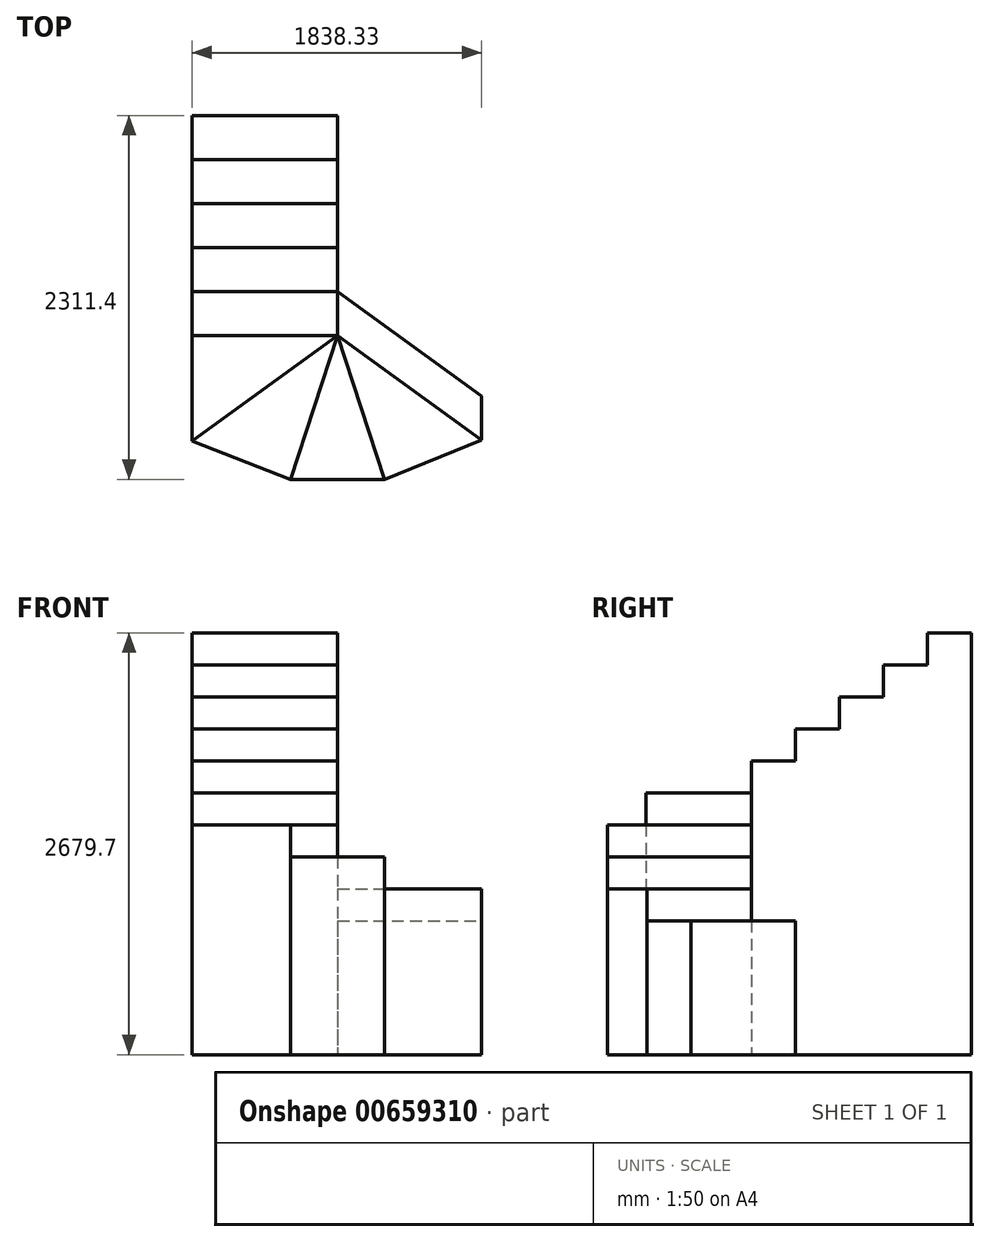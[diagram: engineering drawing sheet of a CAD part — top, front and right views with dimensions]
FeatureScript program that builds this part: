
annotation { "Feature Type Name" : "Feature", "Feature Type Description" : "" }
export const myFeature = defineFeature(function(context is Context, id is Id, definition is map)
    precondition{}
    {
        {
            var Q0;
            Q0=qCreatedBy(makeId("Top.planeOp"),FACE);
            var sketch = newSketch(context, id + "F0", { "sketchPlane" : qUnion([Q0])});
            skLineSegment(sketch, "E0.bottom", {"start": v(0, 0) * mm, "end": v(923.92, 0) * mm});
            skLineSegment(sketch, "E0.top", {"start": v(0, -279.4) * mm, "end": v(923.93, -279.4) * mm});
            skLineSegment(sketch, "E0.left", {"start": v(0, 0) * mm, "end": v(0, -279.4) * mm});
            skLineSegment(sketch, "E0.right", {"start": v(923.92, 0) * mm, "end": v(923.92, -279.4) * mm});
            skLineSegment(sketch, "E1.top", {"start": v(0, -558.8) * mm, "end": v(923.93, -558.8) * mm});
            skLineSegment(sketch, "E1.left", {"start": v(0, -279.4) * mm, "end": v(0, -558.8) * mm});
            skLineSegment(sketch, "E1.right", {"start": v(923.93, -279.4) * mm, "end": v(923.93, -558.8) * mm});
            skLineSegment(sketch, "E2.top", {"start": v(0, -838.2) * mm, "end": v(923.93, -838.2) * mm});
            skLineSegment(sketch, "E2.left", {"start": v(0, -558.8) * mm, "end": v(0, -838.2) * mm});
            skLineSegment(sketch, "E2.right", {"start": v(923.93, -558.8) * mm, "end": v(923.93, -838.2) * mm});
            skLineSegment(sketch, "E3.top", {"start": v(0, -1117.6) * mm, "end": v(923.93, -1117.6) * mm});
            skLineSegment(sketch, "E3.left", {"start": v(0, -838.2) * mm, "end": v(0, -1117.6) * mm});
            skLineSegment(sketch, "E3.right", {"start": v(923.93, -838.2) * mm, "end": v(923.93, -1117.6) * mm});
            skSolve(sketch);
        }
        {
            var Q0;
            Q0=makeQuery(id+"F0.imprint","IMPRINT",FACE,{"disambiguationData":[TD([[makeQuery(id+"F0.imprint","IMPRINT",EDGE,{"derivedFrom":sQuery(id+"F0.wireOp",EDGE,"E0.bottom")}),-1.0]])]});
            extrude(context, id + "F1", {"entities" : qUnion([Q0]), "depth" : 2679.7 * mm, "offsetDistance" : 25.4 * mm});
        }
        {
            var Q0;
            Q0=makeQuery(id+"F1.opExtrude","CAP_FACE",FACE,{"disambiguationData":[OSD([sQuery(id+"F0.wireOp",EDGE,"E0.bottom"),sQuery(id+"F0.wireOp",EDGE,"E0.left"),sQuery(id+"F0.wireOp",EDGE,"E0.right"),sQuery(id+"F0.wireOp",EDGE,"E0.top")])],"isStart":true});
            var sketch = newSketch(context, id + "F2", { "sketchPlane" : qUnion([Q0])});
            skLineSegment(sketch, "E4.bottom", {"start": v(0, 279.4) * mm, "end": v(923.92, 279.4) * mm});
            skLineSegment(sketch, "E4.top", {"start": v(0, 558.8) * mm, "end": v(923.92, 558.8) * mm});
            skLineSegment(sketch, "E4.left", {"start": v(0, 279.4) * mm, "end": v(0, 558.8) * mm});
            skLineSegment(sketch, "E4.right", {"start": v(923.92, 279.4) * mm, "end": v(923.92, 558.8) * mm});
            skSolve(sketch);
        }
        {
            var Q0;
            Q0 = qSketchRegion(id + "F2", true);
            extrude(context, id + "F3", {"entities" : qUnion([Q0]), "operationType" : NewBodyOperationType.ADD, "oppositeDirection" : true, "depth" : 2476.5 * mm, "offsetDistance" : 25.4 * mm});
        }
        {
            var Q0;
            Q0=makeQuery(id+"F3.boolean.opBoolean","MERGE",FACE,{"derivedFrom":[makeQuery(id+"F1.opExtrude","CAP_FACE",FACE,{"disambiguationData":[OSD([sQuery(id+"F0.wireOp",EDGE,"E0.bottom"),sQuery(id+"F0.wireOp",EDGE,"E0.left"),sQuery(id+"F0.wireOp",EDGE,"E0.right"),sQuery(id+"F0.wireOp",EDGE,"E0.top")])],"isStart":true}),makeQuery(id+"F3.opExtrude","CAP_FACE",FACE,{"disambiguationData":[OSD([sQuery(id+"F2.wireOp",EDGE,"E4.bottom"),sQuery(id+"F2.wireOp",EDGE,"E4.top"),sQuery(id+"F2.wireOp",EDGE,"E4.left"),sQuery(id+"F2.wireOp",EDGE,"E4.right")])],"isStart":true})]});
            var sketch = newSketch(context, id + "F4", { "sketchPlane" : qUnion([Q0])});
            skLineSegment(sketch, "E5.bottom", {"start": v(0, 558.8) * mm, "end": v(923.92, 558.8) * mm});
            skLineSegment(sketch, "E5.top", {"start": v(0, 838.2) * mm, "end": v(923.92, 838.2) * mm});
            skLineSegment(sketch, "E5.left", {"start": v(0, 558.8) * mm, "end": v(0, 838.2) * mm});
            skLineSegment(sketch, "E5.right", {"start": v(923.92, 558.8) * mm, "end": v(923.92, 838.2) * mm});
            skSolve(sketch);
        }
        {
            var Q0;
            Q0 = qSketchRegion(id + "F4", true);
            extrude(context, id + "F5", {"entities" : qUnion([Q0]), "operationType" : NewBodyOperationType.ADD, "oppositeDirection" : true, "depth" : 2273.3 * mm, "offsetDistance" : 25.4 * mm});
        }
        {
            var Q0;
            Q0=makeQuery(id+"F5.boolean.opBoolean","MERGE",FACE,{"derivedFrom":[makeQuery(id+"F3.boolean.opBoolean","MERGE",FACE,{"derivedFrom":[makeQuery(id+"F1.opExtrude","CAP_FACE",FACE,{"disambiguationData":[OSD([sQuery(id+"F0.wireOp",EDGE,"E0.bottom"),sQuery(id+"F0.wireOp",EDGE,"E0.left"),sQuery(id+"F0.wireOp",EDGE,"E0.right"),sQuery(id+"F0.wireOp",EDGE,"E0.top")])],"isStart":true}),makeQuery(id+"F3.opExtrude","CAP_FACE",FACE,{"disambiguationData":[OSD([sQuery(id+"F2.wireOp",EDGE,"E4.bottom"),sQuery(id+"F2.wireOp",EDGE,"E4.top"),sQuery(id+"F2.wireOp",EDGE,"E4.left"),sQuery(id+"F2.wireOp",EDGE,"E4.right")])],"isStart":true})]}),makeQuery(id+"F5.opExtrude","CAP_FACE",FACE,{"disambiguationData":[OSD([sQuery(id+"F4.wireOp",EDGE,"E5.bottom"),sQuery(id+"F4.wireOp",EDGE,"E5.top"),sQuery(id+"F4.wireOp",EDGE,"E5.left"),sQuery(id+"F4.wireOp",EDGE,"E5.right")])],"isStart":true})]});
            var sketch = newSketch(context, id + "F6", { "sketchPlane" : qUnion([Q0])});
            skLineSegment(sketch, "E6.bottom", {"start": v(923.92, 838.2) * mm, "end": v(0, 838.2) * mm});
            skLineSegment(sketch, "E6.top", {"start": v(923.92, 1117.6) * mm, "end": v(0, 1117.6) * mm});
            skLineSegment(sketch, "E6.left", {"start": v(923.92, 838.2) * mm, "end": v(923.92, 1117.6) * mm});
            skLineSegment(sketch, "E6.right", {"start": v(0, 838.2) * mm, "end": v(0, 1117.6) * mm});
            skSolve(sketch);
        }
        {
            var Q0;
            Q0 = qSketchRegion(id + "F6", true);
            extrude(context, id + "F7", {"entities" : qUnion([Q0]), "operationType" : NewBodyOperationType.ADD, "oppositeDirection" : true, "depth" : 2070.1 * mm, "offsetDistance" : 25.4 * mm});
        }
        {
            var Q0;
            Q0=makeQuery(id+"F7.boolean.opBoolean","MERGE",FACE,{"derivedFrom":[makeQuery(id+"F5.boolean.opBoolean","MERGE",FACE,{"derivedFrom":[makeQuery(id+"F3.boolean.opBoolean","MERGE",FACE,{"derivedFrom":[makeQuery(id+"F1.opExtrude","CAP_FACE",FACE,{"disambiguationData":[OSD([sQuery(id+"F0.wireOp",EDGE,"E0.bottom"),sQuery(id+"F0.wireOp",EDGE,"E0.left"),sQuery(id+"F0.wireOp",EDGE,"E0.right"),sQuery(id+"F0.wireOp",EDGE,"E0.top")])],"isStart":true}),makeQuery(id+"F3.opExtrude","CAP_FACE",FACE,{"disambiguationData":[OSD([sQuery(id+"F2.wireOp",EDGE,"E4.bottom"),sQuery(id+"F2.wireOp",EDGE,"E4.top"),sQuery(id+"F2.wireOp",EDGE,"E4.left"),sQuery(id+"F2.wireOp",EDGE,"E4.right")])],"isStart":true})]}),makeQuery(id+"F5.opExtrude","CAP_FACE",FACE,{"disambiguationData":[OSD([sQuery(id+"F4.wireOp",EDGE,"E5.bottom"),sQuery(id+"F4.wireOp",EDGE,"E5.top"),sQuery(id+"F4.wireOp",EDGE,"E5.left"),sQuery(id+"F4.wireOp",EDGE,"E5.right")])],"isStart":true})]}),makeQuery(id+"F7.opExtrude","CAP_FACE",FACE,{"disambiguationData":[OSD([sQuery(id+"F6.wireOp",EDGE,"E6.bottom"),sQuery(id+"F6.wireOp",EDGE,"E6.top"),sQuery(id+"F6.wireOp",EDGE,"E6.left"),sQuery(id+"F6.wireOp",EDGE,"E6.right")])],"isStart":true})]});
            var sketch = newSketch(context, id + "F8", { "sketchPlane" : qUnion([Q0])});
            skLineSegment(sketch, "E7.bottom", {"start": v(0, 1117.6) * mm, "end": v(923.92, 1117.6) * mm});
            skLineSegment(sketch, "E7.top", {"start": v(0, 1397) * mm, "end": v(923.92, 1397) * mm});
            skLineSegment(sketch, "E7.left", {"start": v(0, 1117.6) * mm, "end": v(0, 1397) * mm});
            skLineSegment(sketch, "E7.right", {"start": v(923.92, 1117.6) * mm, "end": v(923.92, 1397) * mm});
            skSolve(sketch);
        }
        {
            var Q0;
            Q0 = qSketchRegion(id + "F8", true);
            extrude(context, id + "F9", {"entities" : qUnion([Q0]), "operationType" : NewBodyOperationType.ADD, "oppositeDirection" : true, "depth" : 1866.9 * mm, "offsetDistance" : 25.4 * mm});
        }
        {
            var Q0;
            Q0=makeQuery(id+"F9.boolean.opBoolean","MERGE",FACE,{"derivedFrom":[makeQuery(id+"F7.boolean.opBoolean","MERGE",FACE,{"derivedFrom":[makeQuery(id+"F5.boolean.opBoolean","MERGE",FACE,{"derivedFrom":[makeQuery(id+"F3.boolean.opBoolean","MERGE",FACE,{"derivedFrom":[makeQuery(id+"F1.opExtrude","CAP_FACE",FACE,{"disambiguationData":[OSD([sQuery(id+"F0.wireOp",EDGE,"E0.bottom"),sQuery(id+"F0.wireOp",EDGE,"E0.left"),sQuery(id+"F0.wireOp",EDGE,"E0.right"),sQuery(id+"F0.wireOp",EDGE,"E0.top")])],"isStart":true}),makeQuery(id+"F3.opExtrude","CAP_FACE",FACE,{"disambiguationData":[OSD([sQuery(id+"F2.wireOp",EDGE,"E4.bottom"),sQuery(id+"F2.wireOp",EDGE,"E4.top"),sQuery(id+"F2.wireOp",EDGE,"E4.left"),sQuery(id+"F2.wireOp",EDGE,"E4.right")])],"isStart":true})]}),makeQuery(id+"F5.opExtrude","CAP_FACE",FACE,{"disambiguationData":[OSD([sQuery(id+"F4.wireOp",EDGE,"E5.bottom"),sQuery(id+"F4.wireOp",EDGE,"E5.top"),sQuery(id+"F4.wireOp",EDGE,"E5.left"),sQuery(id+"F4.wireOp",EDGE,"E5.right")])],"isStart":true})]}),makeQuery(id+"F7.opExtrude","CAP_FACE",FACE,{"disambiguationData":[OSD([sQuery(id+"F6.wireOp",EDGE,"E6.bottom"),sQuery(id+"F6.wireOp",EDGE,"E6.top"),sQuery(id+"F6.wireOp",EDGE,"E6.left"),sQuery(id+"F6.wireOp",EDGE,"E6.right")])],"isStart":true})]}),makeQuery(id+"F9.opExtrude","CAP_FACE",FACE,{"disambiguationData":[OSD([sQuery(id+"F8.wireOp",EDGE,"E7.bottom"),sQuery(id+"F8.wireOp",EDGE,"E7.top"),sQuery(id+"F8.wireOp",EDGE,"E7.left"),sQuery(id+"F8.wireOp",EDGE,"E7.right")])],"isStart":true})]});
            var sketch = newSketch(context, id + "F10", { "sketchPlane" : qUnion([Q0])});
            skLineSegment(sketch, "E8", {"start": v(923.92, 2311.4) * mm, "end": v(923.92, 1397) * mm, "construction": true});
            skPoint(sketch, "E9", {"position": v(923.92, 698.5) * mm});
            skLineSegment(sketch, "E10", {"start": v(923.92, 1397) * mm, "end": v(0, 2068.27) * mm});
            skLineSegment(sketch, "E11", {"start": v(0, 1397) * mm, "end": v(0, 2068.27) * mm});
            skSolve(sketch);
        }
        {
            var Q0;
            Q0 = qSketchRegion(id + "F10", true);
            var Q1;
            Q1=makeQuery(id+"F10.imprint","IMPRINT",FACE,{"disambiguationData":[TD([[makeQuery(id+"F10.imprint","IMPRINT",EDGE,{"derivedFrom":sQuery(id+"F10.wireOp",EDGE,"E10")}),1.0]])]});
            extrude(context, id + "F11", {"entities" : qUnion([Q0, Q1]), "oppositeDirection" : true, "depth" : 1663.7 * mm, "offsetDistance" : 25.4 * mm});
        }
        {
            var Q0;
            Q0=makeQuery(id+"F11.opExtrude","CAP_FACE",FACE,{"disambiguationData":[OSD([sQuery(id+"F8.wireOp",EDGE,"E7.top"),sQuery(id+"F10.wireOp",EDGE,"E10"),sQuery(id+"F10.wireOp",EDGE,"E11")])],"isStart":true});
            var sketch = newSketch(context, id + "F12", { "sketchPlane" : qUnion([Q0])});
            skLineSegment(sketch, "E12", {"start": v(923.92, 1397) * mm, "end": v(923.92, 2311.4) * mm, "construction": true});
            skLineSegment(sketch, "E13", {"start": v(923.92, 1397) * mm, "end": v(626.82, 2311.4) * mm});
            skLineSegment(sketch, "E14", {"start": v(626.82, 2311.4) * mm, "end": v(0, 2068.27) * mm});
            skSolve(sketch);
        }
        {
            var Q0;
            Q0 = qSketchRegion(id + "F12", true);
            var Q1;
            Q1=makeQuery(id+"F12.imprint","IMPRINT",FACE,{"disambiguationData":[TD([[makeQuery(id+"F12.imprint","IMPRINT",EDGE,{"derivedFrom":sQuery(id+"F12.wireOp",EDGE,"E13")}),1.0]])]});
            extrude(context, id + "F13", {"entities" : qUnion([Q0, Q1]), "operationType" : NewBodyOperationType.ADD, "oppositeDirection" : true, "depth" : 1460.5 * mm, "offsetDistance" : 25.4 * mm});
        }
        {
            var Q0;
            {var subQ0=sQuery(id+"F10.wireOp",EDGE,"E10");Q0=makeQuery(id+"F13.boolean.opBoolean","MERGE",FACE,{"derivedFrom":[makeQuery(id+"F11.opExtrude","CAP_FACE",FACE,{"disambiguationData":[OSD([sQuery(id+"F8.wireOp",EDGE,"E7.top"),subQ0,sQuery(id+"F10.wireOp",EDGE,"E11")])],"isStart":true}),makeQuery(id+"F13.opExtrude","CAP_FACE",FACE,{"disambiguationData":[OSD([subQ0,sQuery(id+"F12.wireOp",EDGE,"E13"),sQuery(id+"F12.wireOp",EDGE,"E14")])],"isStart":true})]});}
            var sketch = newSketch(context, id + "F14", { "sketchPlane" : qUnion([Q0])});
            skLineSegment(sketch, "E15", {"start": v(923.92, 1397) * mm, "end": v(1221.03, 2311.4) * mm});
            skLineSegment(sketch, "E16", {"start": v(626.82, 2311.4) * mm, "end": v(1221.03, 2311.4) * mm});
            skSolve(sketch);
        }
        {
            var Q0;
            Q0=makeQuery(id+"F14.imprint","IMPRINT",FACE,{"disambiguationData":[TD([[makeQuery(id+"F14.imprint","IMPRINT",EDGE,{"derivedFrom":sQuery(id+"F14.wireOp",EDGE,"E15")}),1.0]])]});
            extrude(context, id + "F15", {"entities" : qUnion([Q0]), "operationType" : NewBodyOperationType.ADD, "oppositeDirection" : true, "depth" : 1257.3 * mm, "offsetDistance" : 25.4 * mm});
        }
        {
            var Q0;
            Q0=makeQuery(id+"F9.boolean.opBoolean","MERGE",FACE,{"derivedFrom":[makeQuery(id+"F7.boolean.opBoolean","MERGE",FACE,{"derivedFrom":[makeQuery(id+"F5.boolean.opBoolean","MERGE",FACE,{"derivedFrom":[makeQuery(id+"F3.boolean.opBoolean","MERGE",FACE,{"derivedFrom":[makeQuery(id+"F1.opExtrude","SWEPT_FACE",FACE,{"disambiguationData":[OSD([sQuery(id+"F0.wireOp",EDGE,"E0.right")])]}),makeQuery(id+"F3.opExtrude","SWEPT_FACE",FACE,{"disambiguationData":[OSD([sQuery(id+"F2.wireOp",EDGE,"E4.right")])]})]}),makeQuery(id+"F5.opExtrude","SWEPT_FACE",FACE,{"disambiguationData":[OSD([sQuery(id+"F4.wireOp",EDGE,"E5.right")])]})]}),makeQuery(id+"F7.opExtrude","SWEPT_FACE",FACE,{"disambiguationData":[OSD([sQuery(id+"F6.wireOp",EDGE,"E6.left")])]})]}),makeQuery(id+"F9.opExtrude","SWEPT_FACE",FACE,{"disambiguationData":[OSD([sQuery(id+"F8.wireOp",EDGE,"E7.right")])]})]});
            cPlane(context, id + "F16", {"entities" : qUnion([Q0]), "cplaneType" : CPlaneType.OFFSET, "offset" : 0 * mm, "width" : 152.4 * mm, "height" : 152.4 * mm});
        }
        {
            var Q0;
            {var subQ0=sQuery(id+"F12.wireOp",EDGE,"E13");var subQ1=sQuery(id+"F10.wireOp",EDGE,"E10");Q0=makeQuery(id+"F15.boolean.opBoolean","MERGE",FACE,{"derivedFrom":[makeQuery(id+"F13.boolean.opBoolean","MERGE",FACE,{"derivedFrom":[makeQuery(id+"F11.opExtrude","CAP_FACE",FACE,{"disambiguationData":[OSD([sQuery(id+"F8.wireOp",EDGE,"E7.top"),subQ1,sQuery(id+"F10.wireOp",EDGE,"E11")])],"isStart":true}),makeQuery(id+"F13.opExtrude","CAP_FACE",FACE,{"disambiguationData":[OSD([subQ1,subQ0,sQuery(id+"F12.wireOp",EDGE,"E14")])],"isStart":true})]}),makeQuery(id+"F15.opExtrude","CAP_FACE",FACE,{"disambiguationData":[OSD([subQ0,sQuery(id+"F14.wireOp",EDGE,"E15"),sQuery(id+"F14.wireOp",EDGE,"E16")])],"isStart":true})]});}
            var sketch = newSketch(context, id + "F17", { "sketchPlane" : qUnion([Q0])});
            skLineSegment(sketch, "E17", {"start": v(923.92, 1397) * mm, "end": v(1838.33, 2061.35) * mm});
            skLineSegment(sketch, "E18", {"start": v(1838.33, 2061.35) * mm, "end": v(1221.03, 2311.4) * mm});
            skSolve(sketch);
        }
        {
            var Q0;
            Q0=makeQuery(id+"F17.imprint","IMPRINT",FACE,{"disambiguationData":[TD([[makeQuery(id+"F17.imprint","IMPRINT",EDGE,{"derivedFrom":sQuery(id+"F17.wireOp",EDGE,"E17")}),1.0]])]});
            extrude(context, id + "F18", {"entities" : qUnion([Q0]), "operationType" : NewBodyOperationType.ADD, "oppositeDirection" : true, "depth" : 1054.1 * mm, "offsetDistance" : 25.4 * mm});
        }
        {
            var Q0;
            {var subQ0=sQuery(id+"F14.wireOp",EDGE,"E15");var subQ1=sQuery(id+"F12.wireOp",EDGE,"E13");var subQ2=sQuery(id+"F10.wireOp",EDGE,"E10");Q0=makeQuery(id+"F18.boolean.opBoolean","MERGE",FACE,{"derivedFrom":[makeQuery(id+"F15.boolean.opBoolean","MERGE",FACE,{"derivedFrom":[makeQuery(id+"F13.boolean.opBoolean","MERGE",FACE,{"derivedFrom":[makeQuery(id+"F11.opExtrude","CAP_FACE",FACE,{"disambiguationData":[OSD([sQuery(id+"F8.wireOp",EDGE,"E7.top"),subQ2,sQuery(id+"F10.wireOp",EDGE,"E11")])],"isStart":true}),makeQuery(id+"F13.opExtrude","CAP_FACE",FACE,{"disambiguationData":[OSD([subQ2,subQ1,sQuery(id+"F12.wireOp",EDGE,"E14")])],"isStart":true})]}),makeQuery(id+"F15.opExtrude","CAP_FACE",FACE,{"disambiguationData":[OSD([subQ1,subQ0,sQuery(id+"F14.wireOp",EDGE,"E16")])],"isStart":true})]}),makeQuery(id+"F18.opExtrude","CAP_FACE",FACE,{"disambiguationData":[OSD([subQ0,sQuery(id+"F17.wireOp",EDGE,"E17"),sQuery(id+"F17.wireOp",EDGE,"E18")])],"isStart":true})]});}
            var sketch = newSketch(context, id + "F19", { "sketchPlane" : qUnion([Q0])});
            skLineSegment(sketch, "E19", {"start": v(1838.33, 2061.35) * mm, "end": v(1838.33, 1781.95) * mm});
            skLineSegment(sketch, "E20", {"start": v(1838.33, 1781.95) * mm, "end": v(923.92, 1117.6) * mm});
            skLineSegment(sketch, "E21", {"start": v(923.92, 1117.6) * mm, "end": v(923.92, 1397) * mm});
            skSolve(sketch);
        }
        {
            var Q0;
            Q0 = qSketchRegion(id + "F19", true);
            var Q1;
            Q1=makeQuery(id+"F19.imprint","IMPRINT",FACE,{"disambiguationData":[TD([[makeQuery(id+"F19.imprint","IMPRINT",EDGE,{"derivedFrom":sQuery(id+"F19.wireOp",EDGE,"E19")}),-1.0]])]});
            extrude(context, id + "F20", {"entities" : qUnion([Q0, Q1]), "oppositeDirection" : true, "depth" : 850.9 * mm, "offsetDistance" : 25.4 * mm});
        }
    });
